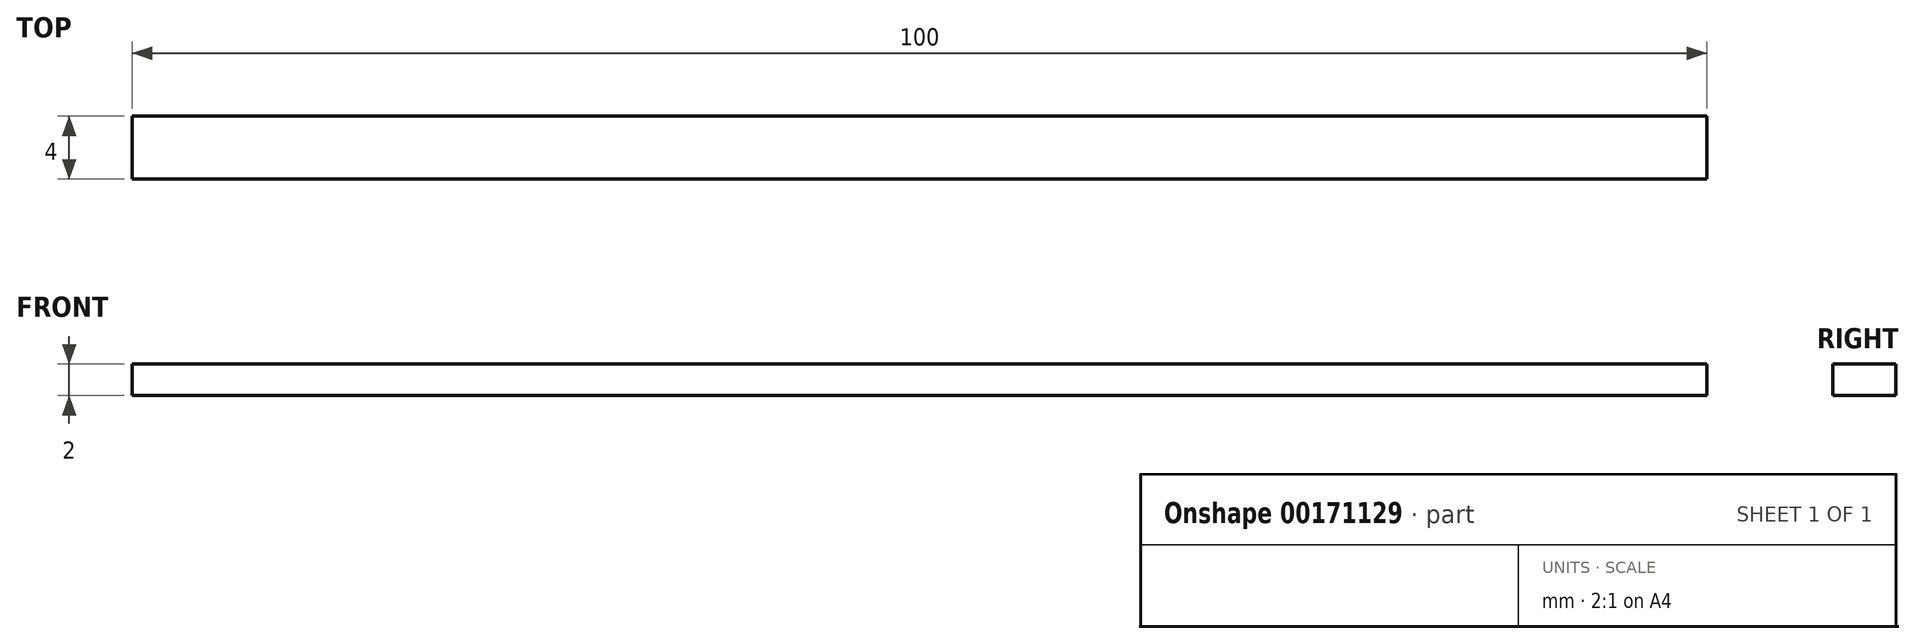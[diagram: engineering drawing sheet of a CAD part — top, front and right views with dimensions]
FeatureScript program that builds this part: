
annotation { "Feature Type Name" : "Feature", "Feature Type Description" : "" }
export const myFeature = defineFeature(function(context is Context, id is Id, definition is map)
    precondition{}
    {
        {
            var Q0;
            Q0=qCreatedBy(makeId("Top.planeOp"),FACE);
            var sketch = newSketch(context, id + "F0", { "sketchPlane" : qUnion([Q0])});
            skLineSegment(sketch, "E0.bottom", {"start": v(-50.81, 23.89) * mm, "end": v(-150.81, 23.89) * mm});
            skLineSegment(sketch, "E0.top", {"start": v(-50.81, 27.89) * mm, "end": v(-150.81, 27.89) * mm});
            skLineSegment(sketch, "E0.left", {"start": v(-50.81, 23.89) * mm, "end": v(-50.81, 27.89) * mm});
            skLineSegment(sketch, "E0.right", {"start": v(-150.81, 23.89) * mm, "end": v(-150.81, 27.89) * mm});
            skPoint(sketch, "E0.middle", {"position": v(-100.81, 25.89) * mm});
            skSolve(sketch);
        }
        {
            var Q0;
            Q0 = qSketchRegion(id + "F0", true);
            extrude(context, id + "F1", {"entities" : qUnion([Q0]), "depth" : 2 * mm});
        }
    });
